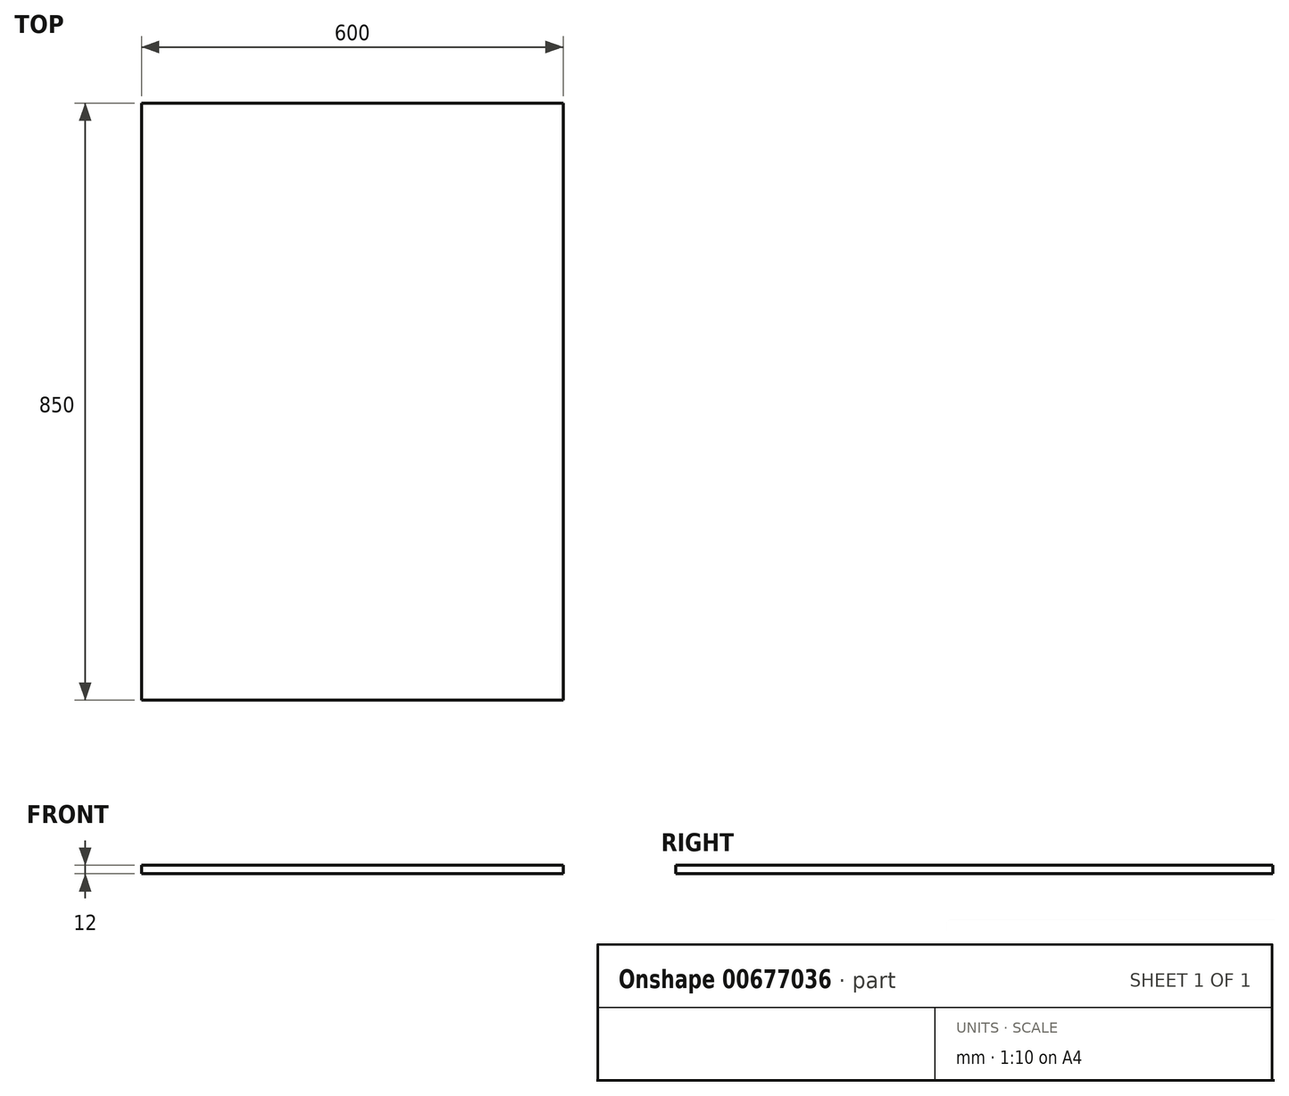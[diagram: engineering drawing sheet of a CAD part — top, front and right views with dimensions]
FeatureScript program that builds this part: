
annotation { "Feature Type Name" : "Feature", "Feature Type Description" : "" }
export const myFeature = defineFeature(function(context is Context, id is Id, definition is map)
    precondition{}
    {
        {
            var Q0;
            Q0=qCreatedBy(makeId("Top.planeOp"),FACE);
            var sketch = newSketch(context, id + "F0", { "sketchPlane" : qUnion([Q0])});
            skLineSegment(sketch, "E0.bottom", {"start": v(-300, 425) * mm, "end": v(300, 425) * mm});
            skLineSegment(sketch, "E0.top", {"start": v(-300, -425) * mm, "end": v(300, -425) * mm});
            skLineSegment(sketch, "E0.left", {"start": v(-300, 425) * mm, "end": v(-300, -425) * mm});
            skLineSegment(sketch, "E0.right", {"start": v(300, 425) * mm, "end": v(300, -425) * mm});
            skSolve(sketch);
        }
        {
            var Q0;
            Q0=makeQuery(id+"F0.imprint","IMPRINT",FACE,{"disambiguationData":[TD([[makeQuery(id+"F0.imprint","IMPRINT",EDGE,{"derivedFrom":sQuery(id+"F0.wireOp",EDGE,"E0.bottom")}),-1.0]])]});
            extrude(context, id + "F1", {"entities" : qUnion([Q0]), "depth" : 12 * mm, "offsetDistance" : 25 * mm});
        }
    });
